# Revit family: Faucet-Deck_Mount-Bath-KALLISTA-Bellis-P24601-1
name_source: partatom
category: Plumbing Fixtures
units: mm (PartAtom-declared; Revit-internal decimal feet)

## family parameters
Cut with Voids When Loaded = No
Host = Face
Maintain Annotation Orientation = No
OmniClass Number = 23.31.11.00
OmniClass Title = Faucets
Part Type = Normal
Room Calculation Point = No
Round Connector Dimension = Use Diameter
Shared = No

## types (4) — shared parameters
ADA Compliant = No
Assembly Code = D2010
CW Connection = Yes
Cold Water Inlet = Cold Water Inlet
Date Modified = 02/04/2025
Default Elevation = 36"
Description = Sink Faucet, Noble Spout, Lever Handles
Drain Included = No
Flow Rate = 1 GPM
HW Connection = Yes
Handle Clearance = 3 1/8"
Height = 3 11/16"
Hot Water Inlet = Hot Water Inlet
Length = 5"
Manufacturer = Kallista Co.
Master Format 2014 = 22 41 39
Master Format 2014 Name = Residential Faucets, Supplies, and Trim
Material = Premium Metal Construction
Pressure = 60.00 psi
Product Documentation Link = https://resources.kohler.com
Product Name = Bellis
Spout Reach = 5"
URL = https://www.kallista.com
Vent Connection = No
Waste Connection = No
Waste Water Outlet = Waste Water Outlet
WaterSense Certified = No

## per-type parameters (varying)
| type | Finish | Model | Product Page URL | Type |
| SA-Antique Silver | Kallista-Metal-SA-Antique_Silver | P24601-SA |  | 1 |
| ULB-Unlaquered Brass | Kallista-Metal-ULB-Unlaquered_Brass | P24601-ULB | https://www.kallista.com | 2 |
| CP-Chrome | Kallista-Metal-CP-Chrome | P24601-CP | https://www.kallista.com | 3 |
| AD-Nickel Silver | Kallista-Metal-AD-Nickel_Silver | P24601-AD | https://www.kallista.com | 4 |

## geometry (parser evidence)
native form markers: Sweep x7
no freeform markers — native parametric forms only
